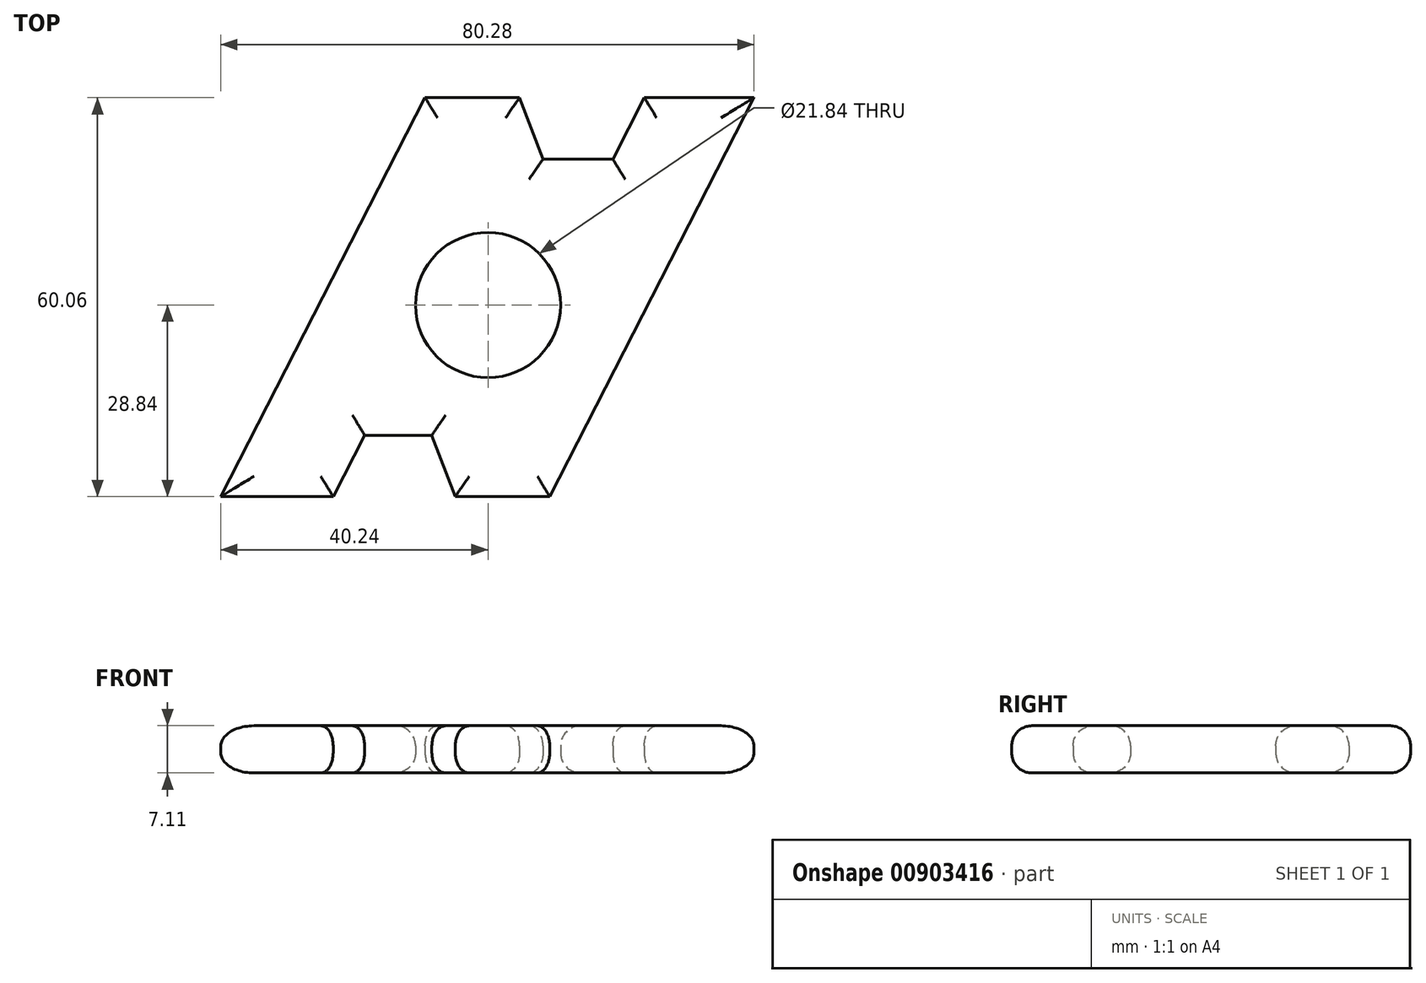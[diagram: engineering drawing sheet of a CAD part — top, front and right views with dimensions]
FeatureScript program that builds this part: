
annotation { "Feature Type Name" : "Feature", "Feature Type Description" : "" }
export const myFeature = defineFeature(function(context is Context, id is Id, definition is map)
    precondition{}
    {
        {
            var Q0;
            Q0=qCreatedBy(makeId("Top.planeOp"),FACE);
            var sketch = newSketch(context, id + "F0", { "sketchPlane" : qUnion([Q0])});
            skCircle(sketch, "E0", {"center": v(0, 0) * mm, "radius": 10.92 * mm});
            skLineSegment(sketch, "E1", {"start": v(0, 50.17) * mm, "end": v(0, -71.25) * mm});
            skLineSegment(sketch, "E2", {"start": v(-35.5, -28.84) * mm, "end": v(-23.31, -28.84) * mm});
            skLineSegment(sketch, "E3", {"start": v(-4.94, -28.84) * mm, "end": v(0, -28.84) * mm});
            skLineSegment(sketch, "E4", {"start": v(-4.74, 31.22) * mm, "end": v(0, 31.22) * mm});
            skPoint(sketch, "E5.orphan", {"position": v(-9.48, 31.22) * mm});
            skLineSegment(sketch, "E6", {"start": v(-8.47, -19.6) * mm, "end": v(-4.94, -28.84) * mm});
            skPoint(sketch, "E7.orphan", {"position": v(-9.48, -28.84) * mm});
            skLineSegment(sketch, "E8.MirrorCS", {"start": v(4.74, 31.22) * mm, "end": v(0, 31.22) * mm});
            skLineSegment(sketch, "E9.MirrorCS", {"start": v(4.94, -28.84) * mm, "end": v(0, -28.84) * mm});
            skLineSegment(sketch, "E10", {"start": v(35.71, 31.22) * mm, "end": v(23.52, 31.22) * mm});
            skLineSegment(sketch, "E11", {"start": v(-23.31, -28.84) * mm, "end": v(-18.58, -19.6) * mm});
            skLineSegment(sketch, "E12", {"start": v(23.52, 31.22) * mm, "end": v(18.79, 21.98) * mm});
            skLineSegment(sketch, "E13", {"start": v(-18.58, -19.6) * mm, "end": v(-8.47, -19.6) * mm});
            skLineSegment(sketch, "E14", {"start": v(4.74, 31.22) * mm, "end": v(8.27, 21.98) * mm});
            skLineSegment(sketch, "E15", {"start": v(8.27, 21.98) * mm, "end": v(18.79, 21.98) * mm});
            skLineSegment(sketch, "E16", {"start": v(-4.74, 31.22) * mm, "end": v(-9.48, 31.22) * mm});
            skLineSegment(sketch, "E17", {"start": v(-9.48, 31.22) * mm, "end": v(-40.24, -28.84) * mm});
            skLineSegment(sketch, "E18", {"start": v(-40.24, -28.84) * mm, "end": v(-35.5, -28.84) * mm});
            skLineSegment(sketch, "E19", {"start": v(4.94, -28.84) * mm, "end": v(9.29, -28.84) * mm});
            skLineSegment(sketch, "E20", {"start": v(9.29, -28.84) * mm, "end": v(40.04, 31.22) * mm});
            skLineSegment(sketch, "E21", {"start": v(40.04, 31.22) * mm, "end": v(35.71, 31.22) * mm});
            skSolve(sketch);
        }
        {
            var Q0;
            Q0=makeQuery(id+"F0.imprint","IMPRINT",FACE,{"disambiguationData":[TD([[makeQuery(id+"F0.imprint","IMPRINT",EDGE,{"derivedFrom":sQuery(id+"F0.wireOp",EDGE,"E2")}),1.0]])]});
            var Q1;
            {var subQ5=sQuery(id+"F0.wireOp",EDGE,"E8.MirrorCS");Q1=makeQuery(id+"F0.imprint","IMPRINT",FACE,{"disambiguationData":[TD([[makeQuery(id+"F0.imprint","IMPRINT",EDGE,{"derivedFrom":subQ5}),1.0]])]});}
            extrude(context, id + "F1", {"entities" : qUnion([Q0, Q1]), "depth" : 7.11 * mm, "offsetDistance" : 25.4 * mm});
        }
        {
            var Q0;
            Q0=makeQuery(id+"F1.opExtrude","CAP_FACE",FACE,{"disambiguationData":[OSD([sQuery(id+"F0.wireOp",EDGE,"E0"),sQuery(id+"F0.wireOp",EDGE,"E2"),sQuery(id+"F0.wireOp",EDGE,"E3"),sQuery(id+"F0.wireOp",EDGE,"E4"),sQuery(id+"F0.wireOp",EDGE,"E6"),sQuery(id+"F0.wireOp",EDGE,"E8.MirrorCS"),sQuery(id+"F0.wireOp",EDGE,"E9.MirrorCS"),sQuery(id+"F0.wireOp",EDGE,"E10"),sQuery(id+"F0.wireOp",EDGE,"E11"),sQuery(id+"F0.wireOp",EDGE,"E12"),sQuery(id+"F0.wireOp",EDGE,"E13"),sQuery(id+"F0.wireOp",EDGE,"E14"),sQuery(id+"F0.wireOp",EDGE,"E15"),sQuery(id+"F0.wireOp",EDGE,"E16"),sQuery(id+"F0.wireOp",EDGE,"E17"),sQuery(id+"F0.wireOp",EDGE,"E18"),sQuery(id+"F0.wireOp",EDGE,"E19"),sQuery(id+"F0.wireOp",EDGE,"E20"),sQuery(id+"F0.wireOp",EDGE,"E21")])],"isStart":false});
            var Q1;
            Q1=makeQuery(id+"F1.opExtrude","CAP_FACE",FACE,{"disambiguationData":[OSD([sQuery(id+"F0.wireOp",EDGE,"E0"),sQuery(id+"F0.wireOp",EDGE,"E2"),sQuery(id+"F0.wireOp",EDGE,"E3"),sQuery(id+"F0.wireOp",EDGE,"E4"),sQuery(id+"F0.wireOp",EDGE,"E6"),sQuery(id+"F0.wireOp",EDGE,"E8.MirrorCS"),sQuery(id+"F0.wireOp",EDGE,"E9.MirrorCS"),sQuery(id+"F0.wireOp",EDGE,"E10"),sQuery(id+"F0.wireOp",EDGE,"E11"),sQuery(id+"F0.wireOp",EDGE,"E12"),sQuery(id+"F0.wireOp",EDGE,"E13"),sQuery(id+"F0.wireOp",EDGE,"E14"),sQuery(id+"F0.wireOp",EDGE,"E15"),sQuery(id+"F0.wireOp",EDGE,"E16"),sQuery(id+"F0.wireOp",EDGE,"E17"),sQuery(id+"F0.wireOp",EDGE,"E18"),sQuery(id+"F0.wireOp",EDGE,"E19"),sQuery(id+"F0.wireOp",EDGE,"E20"),sQuery(id+"F0.wireOp",EDGE,"E21")])],"isStart":true});
            fillet(context, id + "F2", {"entities" : qUnion([Q0, Q1]), "radius" : 3.05 * mm, "tangentPropagation" : true, "allowEdgeOverflow" : false});
        }
    });
